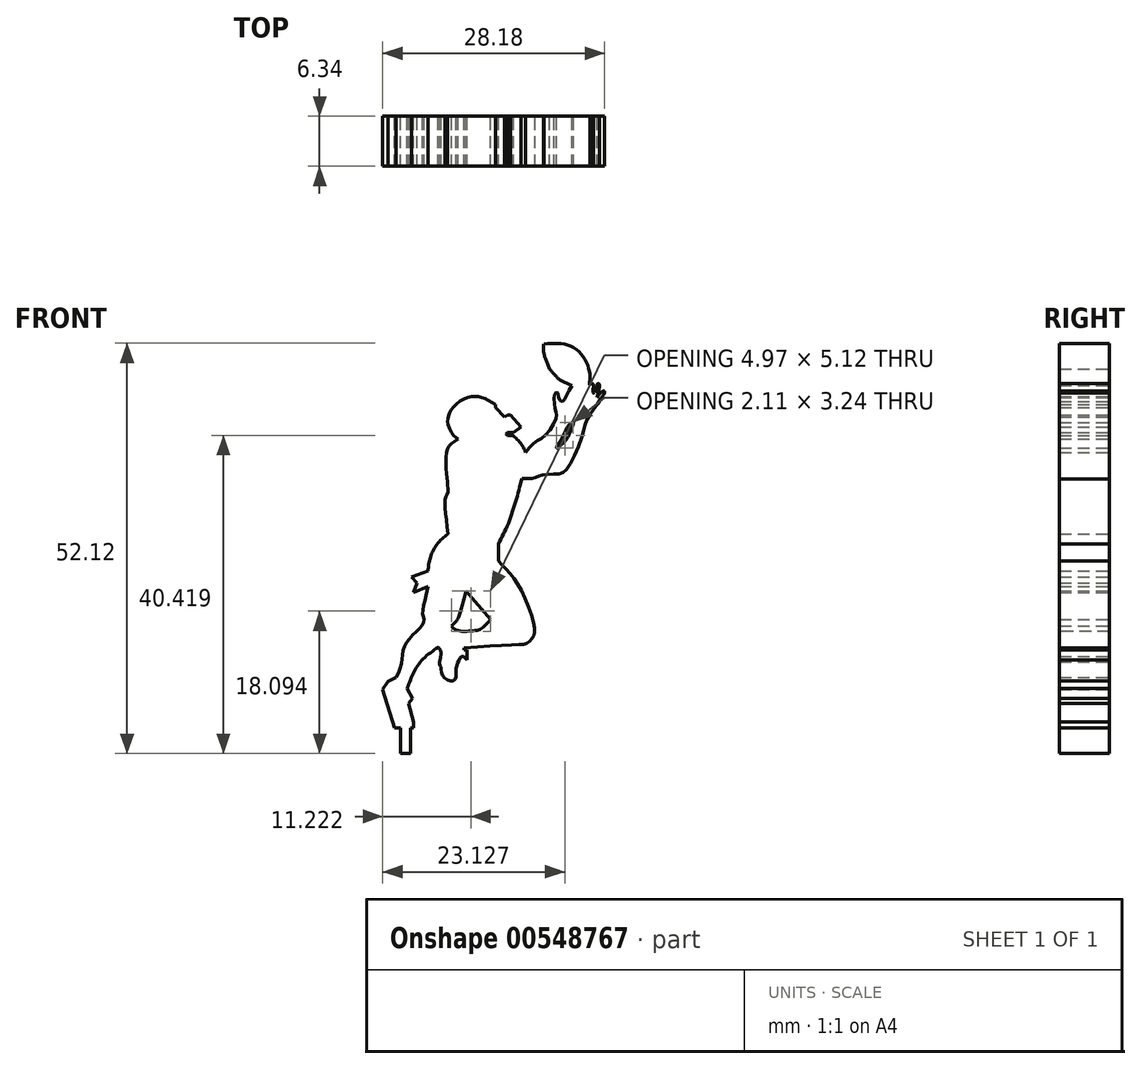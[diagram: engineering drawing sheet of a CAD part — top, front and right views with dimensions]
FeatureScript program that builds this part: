
annotation { "Feature Type Name" : "Feature", "Feature Type Description" : "" }
export const myFeature = defineFeature(function(context is Context, id is Id, definition is map)
    precondition{}
    {
        {
            var Q0;
            Q0=qCreatedBy(makeId("Front.planeOp"),FACE);
            var sketch = newSketch(context, id + "F0", { "sketchPlane" : qUnion([Q0])});
            skLineSegment(sketch, "E0", {"start": v(-24.34, 0) * mm, "end": v(-26.77, 0) * mm});
            skLineSegment(sketch, "E1", {"start": v(-26.77, 0) * mm, "end": v(-28.28, 4.9) * mm});
            skLineSegment(sketch, "E2", {"start": v(-28.28, 4.9) * mm, "end": v(-27.6, 5.9) * mm});
            skLineSegment(sketch, "E3", {"start": v(-27.6, 5.9) * mm, "end": v(-26.58, 6.43) * mm});
            skLineSegment(sketch, "E4", {"start": v(-24.34, 0) * mm, "end": v(-24.34, 0.8) * mm});
            skLineSegment(sketch, "E5", {"start": v(-24.34, 0.8) * mm, "end": v(-25.02, 3.14) * mm});
            skLineSegment(sketch, "E6", {"start": v(-25.02, 3.14) * mm, "end": v(-24.51, 3.73) * mm});
            skLineSegment(sketch, "E7", {"start": v(-24.51, 3.73) * mm, "end": v(-25.18, 5.01) * mm});
            skFitSpline(sketch, "E8", {"points": [v(-25.18, 5.01) * mm, v(-24.37, 6.98) * mm, v(-23.1, 8.8) * mm, v(-21.22, 10.25) * mm], "startDerivative": vector(2.29, 6.12) * mm, "endDerivative": vector(5.87, 3.9) * mm});
            skFitSpline(sketch, "E9", {"points": [v(-21.22, 10.25) * mm, v(-20.9, 9.75) * mm, v(-21.05, 8.36) * mm], "startDerivative": vector(1, -1.07) * mm, "endDerivative": vector(-0.56, -2.6) * mm});
            skFitSpline(sketch, "E10", {"points": [v(-21.05, 8.36) * mm, v(-21.05, 8) * mm, v(-20.89, 7.76) * mm, v(-20.8, 6.98) * mm, v(-20.05, 6.12) * mm, v(-19.23, 6.04) * mm, v(-18.96, 6.62) * mm, v(-18.94, 7.55) * mm, v(-18.7, 8.36) * mm, v(-18.35, 9) * mm, v(-18.06, 9.08) * mm, v(-17.57, 8.64) * mm], "startDerivative": vector(-0.91, -5.86) * mm, "endDerivative": vector(5.44, -6.45) * mm});
            skLineSegment(sketch, "E11", {"start": v(-17.57, 8.64) * mm, "end": v(-17.57, 9.94) * mm});
            skLineSegment(sketch, "E12", {"start": v(-17.57, 9.94) * mm, "end": v(-17.95, 9.94) * mm});
            skLineSegment(sketch, "E13", {"start": v(-17.95, 9.94) * mm, "end": v(-17.95, 10.19) * mm});
            skFitSpline(sketch, "E14", {"points": [v(-17.95, 10.19) * mm, v(-10.8, 10.6) * mm, v(-10, 10.73) * mm, v(-9.32, 11.34) * mm, v(-9, 11.97) * mm, v(-9.06, 13.23) * mm, v(-10.58, 17.3) * mm, v(-12.24, 19.78) * mm, v(-13.6, 21.2) * mm], "startDerivative": vector(39.27, 2.47) * mm, "endDerivative": vector(-11.38, 11.2) * mm});
            skLineSegment(sketch, "E15", {"start": v(-13.6, 21.2) * mm, "end": v(-13.6, 23.38) * mm});
            skFitSpline(sketch, "E16", {"points": [v(-13.6, 23.38) * mm, v(-12.45, 25.68) * mm, v(-11.35, 28.87) * mm, v(-10.6, 31.7) * mm], "startDerivative": vector(3.82, 6.95) * mm, "endDerivative": vector(2.12, 8.31) * mm});
            skFitSpline(sketch, "E17", {"points": [v(-10.6, 31.7) * mm, v(-9.26, 31.7) * mm, v(-8.53, 31.98) * mm, v(-7.64, 32.18) * mm, v(-5.8, 32.3) * mm, v(-4.92, 32.86) * mm, v(-3.05, 36.74) * mm, v(-2.38, 39.09) * mm, v(-1.2, 40.88) * mm, v(-0.23, 42.35) * mm, v(-0.11, 42.57) * mm], "startDerivative": vector(15.45, -1.24) * mm, "endDerivative": vector(2.16, 4.15) * mm});
            skFitSpline(sketch, "E18", {"points": [v(-0.11, 42.57) * mm, v(-0.11, 42.75) * mm, v(-0.27, 42.82) * mm, v(-1.04, 41.95) * mm], "startDerivative": vector(0.17, 0.9) * mm, "endDerivative": vector(-1.54, -2.18) * mm});
            skFitSpline(sketch, "E19", {"points": [v(-1.04, 41.95) * mm, v(-0.84, 42.88) * mm, v(-0.75, 43.54) * mm, v(-0.87, 43.76) * mm, v(-1.04, 43.64) * mm, v(-1.42, 42.57) * mm, v(-1.56, 42.57) * mm, v(-1.57, 43) * mm, v(-1.54, 43.59) * mm, v(-1.75, 43.8) * mm, v(-2.03, 43.53) * mm, v(-2.02, 43.53) * mm], "startDerivative": vector(1.37, 6.7) * mm, "endDerivative": vector(0.92, 0.32) * mm});
            skFitSpline(sketch, "E20", {"points": [v(-2.02, 43.53) * mm, v(-2.02, 45.3) * mm, v(-3.03, 47.46) * mm, v(-5.07, 48.73) * mm, v(-7.81, 48.78) * mm], "startDerivative": vector(0.75, 7.8) * mm, "endDerivative": vector(-10.42, -0.87) * mm});
            skFitSpline(sketch, "E21", {"points": [v(-7.81, 48.78) * mm, v(-7.81, 47.69) * mm, v(-7.07, 45.62) * mm], "startDerivative": vector(-0.26, -2.47) * mm, "endDerivative": vector(1.65, -3.79) * mm});
            skFitSpline(sketch, "E22", {"points": [v(-7.07, 45.62) * mm, v(-5.77, 44.25) * mm, v(-4.25, 43.53) * mm], "startDerivative": vector(2.36, -2.97) * mm, "endDerivative": vector(3.28, -1.19) * mm});
            skFitSpline(sketch, "E23", {"points": [v(-4.25, 43.53) * mm, v(-5.1, 41.95) * mm, v(-5.47, 41.48) * mm, v(-5.84, 41.75) * mm, v(-6.04, 42.57) * mm, v(-6.32, 42.57) * mm, v(-6.52, 42.18) * mm, v(-6.4, 40.7) * mm, v(-6.22, 39.98) * mm, v(-6.3, 39.3) * mm, v(-7.61, 37.17) * mm, v(-8.79, 36.4) * mm, v(-10.1, 35.02) * mm], "startDerivative": vector(-8.37, -15.4) * mm, "endDerivative": vector(-11.4, -13.74) * mm});
            skFitSpline(sketch, "E24", {"points": [v(-10.1, 35.02) * mm, v(-10.63, 35.98) * mm, v(-11.28, 36.74) * mm, v(-11.9, 37.17) * mm, v(-12.32, 37.17) * mm, v(-12.6, 37.37) * mm, v(-12.46, 37.5) * mm, v(-12.33, 37.5) * mm], "startDerivative": vector(-2.31, 4.74) * mm, "endDerivative": vector(1.56, -0.32) * mm});
            skLineSegment(sketch, "E25", {"start": v(-12.33, 37.5) * mm, "end": v(-11.66, 37.5) * mm});
            skLineSegment(sketch, "E26", {"start": v(-11.66, 37.5) * mm, "end": v(-10.7, 38.26) * mm});
            skLineSegment(sketch, "E27", {"start": v(-10.7, 38.26) * mm, "end": v(-12.06, 39.77) * mm});
            skLineSegment(sketch, "E28", {"start": v(-12.06, 39.77) * mm, "end": v(-12.44, 39.77) * mm});
            skLineSegment(sketch, "E29", {"start": v(-12.44, 39.77) * mm, "end": v(-12.8, 39.5) * mm});
            skLineSegment(sketch, "E30", {"start": v(-12.8, 39.5) * mm, "end": v(-13.94, 40.73) * mm});
            skLineSegment(sketch, "E31", {"start": v(-13.94, 40.73) * mm, "end": v(-13.94, 41.09) * mm});
            skFitSpline(sketch, "E32", {"points": [v(-13.94, 41.09) * mm, v(-15.4, 41.87) * mm, v(-16.52, 42.12) * mm, v(-18, 41.8) * mm, v(-19.48, 40.51) * mm, v(-19.94, 39.58) * mm, v(-20, 38.77) * mm, v(-19.32, 37.25) * mm, v(-18.74, 36.7) * mm], "startDerivative": vector(-10.72, 6.29) * mm, "endDerivative": vector(5.81, -4.24) * mm});
            skFitSpline(sketch, "E33", {"points": [v(-18.74, 36.7) * mm, v(-19.78, 35.88) * mm, v(-20.17, 34.83) * mm, v(-20.17, 32.32) * mm, v(-20.03, 30.92) * mm, v(-20.03, 29.9) * mm, v(-20.25, 29.38) * mm, v(-20.35, 28.33) * mm, v(-19.99, 24.64) * mm], "startDerivative": vector(-9.93, -6.65) * mm, "endDerivative": vector(2.53, -21.15) * mm});
            skFitSpline(sketch, "E34", {"points": [v(-19.99, 24.64) * mm, v(-21.07, 23.7) * mm, v(-21.96, 22.36) * mm, v(-22.39, 21.06) * mm, v(-22.51, 19.94) * mm], "startDerivative": vector(-4.4, -3.37) * mm, "endDerivative": vector(-0.35, -4.9) * mm});
            skLineSegment(sketch, "E35", {"start": v(-22.51, 19.94) * mm, "end": v(-24.63, 19.17) * mm});
            skLineSegment(sketch, "E36", {"start": v(-24.63, 19.17) * mm, "end": v(-23.93, 18.4) * mm});
            skLineSegment(sketch, "E37", {"start": v(-23.93, 18.4) * mm, "end": v(-24.36, 17.22) * mm});
            skLineSegment(sketch, "E38", {"start": v(-24.36, 17.22) * mm, "end": v(-22.51, 17.97) * mm});
            skFitSpline(sketch, "E39", {"points": [v(-22.51, 17.97) * mm, v(-22.9, 16.3) * mm, v(-23.2, 14.62) * mm, v(-23.07, 13.95) * mm, v(-23.11, 13.28) * mm, v(-23.93, 12.31) * mm, v(-25.12, 11.01) * mm, v(-25.71, 9.67) * mm, v(-25.88, 8.16) * mm, v(-26.58, 6.43) * mm], "startDerivative": vector(-2.99, -12.97) * mm, "endDerivative": vector(-6.67, -13.4) * mm});
            skFitSpline(sketch, "E40", {"points": [v(-17.69, 17.4) * mm, v(-18.26, 15.25) * mm, v(-18.77, 13.83) * mm, v(-19.54, 12.94) * mm], "startDerivative": vector(-1.51, -5.71) * mm, "endDerivative": vector(-2.99, -2.85) * mm});
            skFitSpline(sketch, "E41", {"points": [v(-19.54, 12.94) * mm, v(-18.8, 12.38) * mm, v(-16.96, 12.33) * mm, v(-15.77, 12.6) * mm, v(-14.57, 13.78) * mm], "startDerivative": vector(2.96, -3.29) * mm, "endDerivative": vector(4.29, 5.19) * mm});
            skFitSpline(sketch, "E42", {"points": [v(-14.57, 13.78) * mm, v(-17.69, 17.4) * mm], "startDerivative": vector(-3.12, 3.63) * mm, "endDerivative": vector(-3.12, 3.63) * mm});
            skFitSpline(sketch, "E43", {"points": [v(-4.1, 38.79) * mm, v(-4.6, 38.52) * mm, v(-5.31, 37.17) * mm, v(-6.22, 35.56) * mm, v(-5.2, 36.36) * mm, v(-4.33, 37.9) * mm, v(-4.1, 38.79) * mm]});
            skLineSegment(sketch, "E44", {"start": v(-24.34, 0) * mm, "end": v(-24.73, 0) * mm});
            skLineSegment(sketch, "E45", {"start": v(-24.73, 0) * mm, "end": v(-24.73, -3.25) * mm});
            skLineSegment(sketch, "E46", {"start": v(-24.73, -3.25) * mm, "end": v(-26.01, -3.25) * mm});
            skLineSegment(sketch, "E47", {"start": v(-26.01, -3.25) * mm, "end": v(-26.01, 0) * mm});
            skLineSegment(sketch, "E48", {"start": v(-26.01, 0) * mm, "end": v(-26.77, 0) * mm});
            skSolve(sketch);
        }
        {
            var Q0;
            Q0 = qSketchRegion(id + "F0", true);
            extrude(context, id + "F1", {"entities" : qUnion([Q0]), "depth" : 6.34 * mm, "offsetDistance" : 25 * mm});
        }
    });
